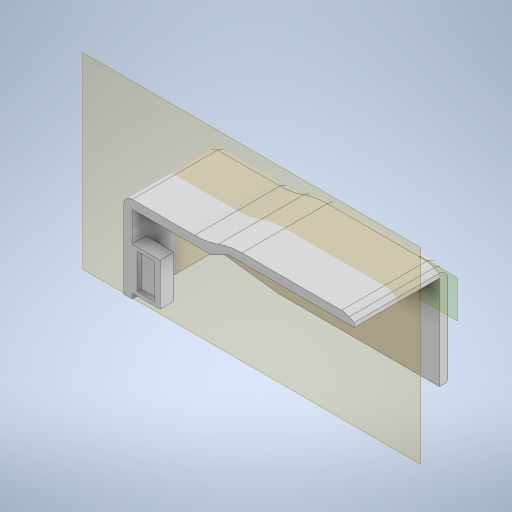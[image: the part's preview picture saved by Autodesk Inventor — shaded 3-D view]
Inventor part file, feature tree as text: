
AUTODESK INVENTOR PART (.ipt)
format: ipt  version: 2023 (Build 270158000, 158)  size: 681,984 bytes
history: native  units: in
note: dims shown in document units (in); Inventor stores cm internally (conversion verified against a paired STEP export)
features: sketch x33, extrude x32, fillet x10, plane x5, chamfer x3, projected_geometry x3, mirror x2
ambient origin geometry x8: Origin, YZ Plane, XZ Plane, XY Plane, X Axis, Y Axis, Z Axis, Center Point
bodies: Solid1 (feature_tree)
feature tree (88):
  extrude  "Extrusion1"  Depth=2.3622in
  sketch  "Sketch2"  dims[d2=2.3622in d3=0.0in d4=3.5433in d5=0.1969in d6=0.0in]
  extrude  "Extrusion2"  Depth=3.5433in
  chamfer  "Chamfer2"  Distance=0.1969in
  extrude  "Extrusion6"  Depth=1.5748in
  extrude  "Extrusion7"  Depth=0.1969in
  plane  "Work Plane1"
  fillet  "Fillet6"  Radius=0.3937in
  fillet  "Fillet9"  Radius=0.1969in
  fillet  "Fillet21"  Radius=0.1969in
  fillet  "Fillet22"  Radius=0.1969in
  chamfer  "Chamfer3"  Distance=2.1654in
  fillet  "Fillet23"  Radius=0.1969in
  fillet  "Fillet24"  Radius=0.1969in
  chamfer  "Chamfer4"  Distance=0.3937in Angle=45.0deg
  fillet  "Fillet25"  Radius=0.1969in
  fillet  "Fillet26"  Radius=0.3937in
  fillet  "Fillet27"  Radius=1.2795in
  plane  "Work Plane7"
  extrude  "Extrusion21"  Depth=0.3937in
  extrude  "Extrusion24"  Depth=0.1969in
  extrude  "Extrusion25"  TaperAngle=0.0deg  [1 undecoded]
  extrude  "Extrusion26"  Depth=0.1969in
  extrude  "Extrusion27"  Depth=0.3937in TaperAngle=0.0deg
  extrude  "Extrusion29"  Depth=0.3937in TaperAngle=0.0deg
  plane  "Work Plane4"
  extrude  "Extrusion30"  Depth=0.1181in
  extrude  "Extrusion31"  Depth=0.0984in
  extrude  "Extrusion32"  Depth=0.3937in
  extrude  "Extrusion33"  Depth=0.3937in TaperAngle=0.0deg
  plane  "Work Plane6"
  extrude  "Extrusion36"  Depth=1.7717in
  extrude  "Extrusion37"  Depth=0.1969in
  extrude  "Extrusion38"  Depth=0.7087in
  mirror  "Mirror1"
  extrude  "Extrusion39"  Depth=0.4724in TaperAngle=0.0deg
  mirror  "Mirror2"
  extrude  "Extrusion40"  Depth=0.1378in
  extrude  "Extrusion41"  Depth=0.1378in
  extrude  "Extrusion42"  Depth=0.1969in TaperAngle=0.0deg
  fillet  "Fillet29"  [1 undecoded]
  sketch  "Sketch50"  dims[d164=0.2756in d166=0.7087in]
  sketch  "Sketch51"  dims[d167=1.4961in d168=0.4724in d169=0.0in]
  extrude  "Extrusion43"  Depth=0.3937in
  extrude  "Extrusion44"  Depth=0.1969in TaperAngle=0.0deg
  extrude  "Extrusion45"  Depth=0.3937in
  extrude  "Extrusion46"  TaperAngle=45.0deg  [1 undecoded]
  extrude  "Extrusion47"  Depth=0.1969in TaperAngle=0.0deg
  extrude  "Extrusion48"  TaperAngle=45.0deg  [1 undecoded]
  extrude  "Extrusion49"  Depth=0.1969in TaperAngle=0.0deg
  extrude  "Extrusion50"  Depth=0.315in
  extrude  "Extrusion51"  Depth=0.1969in TaperAngle=0.0deg
  extrude  "Extrusion52"  Depth=0.3937in TaperAngle=0.0deg
  extrude  "Extrusion53"  Depth=0.1969in TaperAngle=0.0deg
  sketch  "Sketch1"  dims[d0=5.5118in d1=2.3622in]
  sketch  "Sketch3"  dims[d10=0.1969in d11=1.5748in d12=45.0deg d26=1.0433in]
  sketch  "Sketch8"  dims[d27=1.2795in d28=1.1811in d29=0.3937in d30=0.0in d35=0.1969in d36=0.1969in d37=0.1969in]
  sketch  "Sketch9"  dims[d38=0.1969in]
  sketch  "Sketch24"  dims[d39=0.1969in]
  sketch  "Sketch27"  dims[d40=0.1969in]
  sketch  "Sketch28"  dims[d41=0.1969in d42=2.1654in d43=0.0in d66=0.1969in d69=0.1969in]
  sketch  "Sketch29"  dims[d81=1.5748in]
  sketch  "Sketch30"  dims[d82=1.5748in d83=0.3937in d84=0.1969in d85=45.0deg d86=0.1969in d87=0.3937in d88=1.2795in]
  sketch  "Sketch32"  dims[d89=0.1969in d90=0.3937in d91=45.0deg d92=0.3937in]
  sketch  "Sketch34"  dims[d93=0.1969in d94=0.1969in]
  sketch  "Sketch35"  dims[d129=0.1969in d130=0.0in d137=0.0in]
  sketch  "Sketch37"  dims[d138=0.748in d139=0.1969in]
  sketch  "Sketch38"  dims[d140=0.1969in d141=0.3937in d142=0.0in]
  projected_geometry  "Projected Loop4"
  plane  "Work Plane5"
  sketch  "Sketch42"  dims[d143=0.1969in d144=0.3937in d145=0.0in]
  sketch  "Sketch43"  dims[d146=0.1772in d147=0.1181in]
  sketch  "Sketch44"  dims[d148=0.0984in d149=0.0984in]
  sketch  "Sketch45"  dims[d150=0.3937in d151=0.0in d152=0.0984in]
  sketch  "Sketch46"  dims[d153=0.2756in d154=0.3937in d155=0.0in]
  sketch  "Sketch47"  dims[d158=1.122in d159=1.7717in]
  projected_geometry  "Projected Loop5"
  sketch  "Sketch48"  dims[d160=0.1969in d161=0.0in d163=0.2756in]
  sketch  "Sketch52"  dims[d170=0.1575in d171=0.1378in]
  sketch  "Sketch53"  dims[d172=0.1378in d173=0.1378in]
  sketch  "Sketch54"  dims[d174=0.1969in d175=0.0in d176=0.4724in d177=0.0in d178=0.0in]
  sketch  "Sketch55"  dims[d179=0.3937in d180=0.0in d193=0.5906in]
  sketch  "Sketch56"  dims[d194=0.5118in d195=0.1969in d196=0.0in]
  sketch  "Sketch57"  dims[d197=0.4724in d199=0.3937in]
  sketch  "Sketch58"  dims[d200=0.0984in d201=0.0in d202=45.0deg]
  sketch  "Sketch59"  dims[d203=45.0deg d204=0.1969in d205=0.0in]
  sketch  "Sketch60"  dims[d206=45.0deg d207=45.0deg d208=0.1969in d209=0.0in d210=0.315in d211=0.1969in d212=0.0in d213=0.3937in d214=0.0in d215=0.1969in d216=0.0in d217=0.1969in d218=1.9685in d219=0.0in d220=1.9685in d221=0.0in d222=0.3937in d223=0.0in d224=7.874in d225=0.0in d226=0.3937in d227=0.0in d228=0.3937in d229=0.0in d230=0.0in d231=0.0in d232=0.9843in d233=0.6102in d234=0.1969in d235=0.7874in d236=0.1063in d237=0.0in d238=0.315in d239=0.1181in d240=0.0in d241=0.9843in d242=0.8661in d243=0.0in d245=0.315in d246=0.4055in d247=0.7992in d248=0.0925in d249=0.0925in d250=0.0866in d251=0.0in d252=0.2244in d253=0.0in d109=0.0197in d110=0.0344in d111=0.0197in d112=0.0344in d131=0.0197in d132=0.0344in d133=0.0197in d134=0.0344in]
  projected_geometry  "Projected Loop6"
note: 4 required parameter values undecoded (feature->parameter linkage not recoverable at this tier; creation-order binding heuristic only, values carry confidence <= 0.55)
